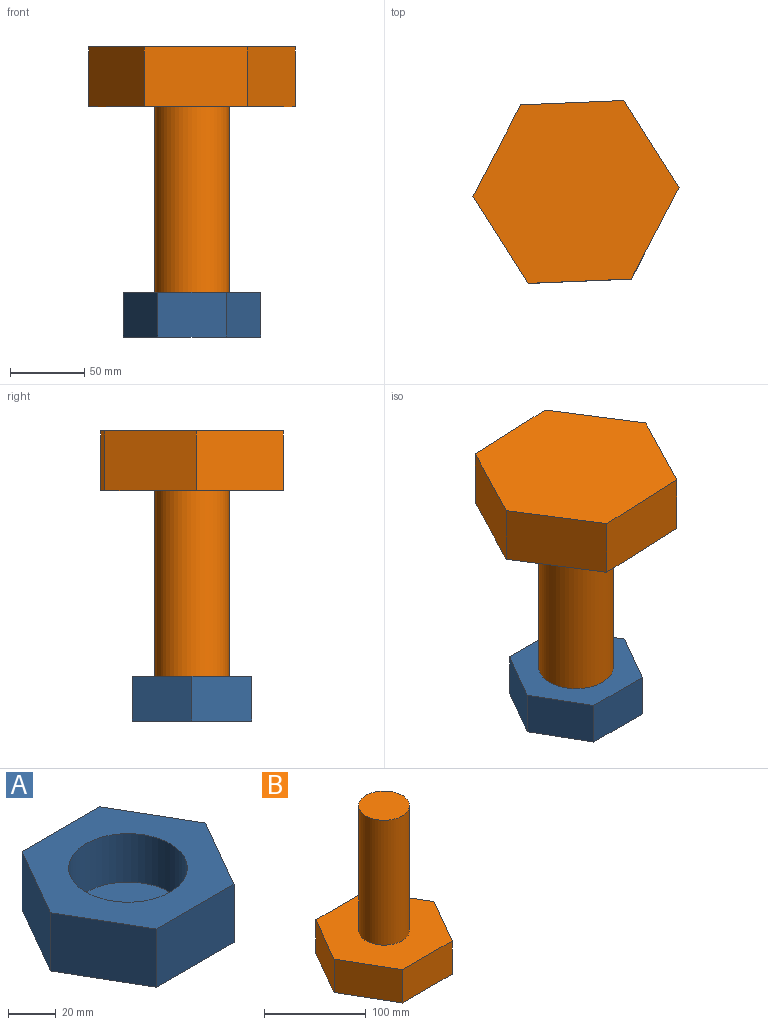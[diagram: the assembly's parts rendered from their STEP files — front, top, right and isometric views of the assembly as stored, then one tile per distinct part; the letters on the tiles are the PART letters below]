
ASSEMBLY  parts=2 mates=1
PART A: 10 faces, bbox 92.4x80x30 mm
  f0: plane 40x30mm, normal (-0.87,0.5,0), area 1385.6mm2, adj f1,f5,f6,f7
  f1: plane 40x30mm, normal (-0.87,-0.5,0), area 1385.6mm2, adj f0,f2,f6,f7
  f2: plane 46.19x30mm, normal (0,-1,0), area 1385.6mm2, adj f1,f3,f6,f7
  f3: plane 40x30mm, normal (0.87,-0.5,0), area 1385.6mm2, adj f2,f4,f6,f7
  f4: plane 40x30mm, normal (0.87,0.5,0), area 1385.6mm2, adj f3,f5,f6,f7
  f5: plane 46.19x30mm, normal (0,1,0), area 1385.6mm2, adj f0,f4,f6,f7
  f6: plane 92.38x80mm, normal (0,0,1), area 3579.1mm2, adj f0,f1,f2,f3,f4,f5,f8
  f7: plane 92.38x80mm, normal (0,0,-1), area 5542.6mm2, adj f0,f1,f2,f3,f4,f5
  f8: cylinder r=25mm len=50mm, axis (0,0,1), area 3927mm2, adj f6,f9
  f9: plane 50x50mm, normal (0,0,1), area 1963.5mm2, adj f8
PART B: 10 faces, bbox 138.6x120x190 mm
  f0: plane 60x40mm, normal (-0.87,0.5,0), area 2771.3mm2, adj f1,f5,f6,f7
  f1: plane 60x40mm, normal (-0.87,-0.5,0), area 2771.3mm2, adj f0,f2,f6,f7
  f2: plane 69.28x40mm, normal (0,-1,0), area 2771.3mm2, adj f1,f3,f6,f7
  f3: plane 60x40mm, normal (0.87,-0.5,0), area 2771.3mm2, adj f2,f4,f6,f7
  f4: plane 60x40mm, normal (0.87,0.5,0), area 2771.3mm2, adj f3,f5,f6,f7
  f5: plane 69.28x40mm, normal (0,1,0), area 2771.3mm2, adj f0,f4,f6,f7
  f6: plane 138.56x120mm, normal (0,0,1), area 10507.3mm2, adj f0,f1,f2,f3,f4,f5,f8
  f7: plane 138.56x120mm, normal (0,0,-1), area 12470.8mm2, adj f0,f1,f2,f3,f4,f5
  f8: cylinder r=25mm len=150mm, axis (0,0,-1), area 23561.9mm2, adj f6,f9
  f9: plane 50x50mm, normal (0,0,1), area 1963.5mm2, adj f8
PLACE A t=(-25.27,-13.23,-12.96)mm fixed
PLACE B rot(axis=(-1,-0.02,0),180deg) t=(-25.27,-13.23,181.87)mm
MATE cylindrical A.f8 <-> B.f8  axis (0,0,1) through (-25.27,-13.23,17.04)mm
